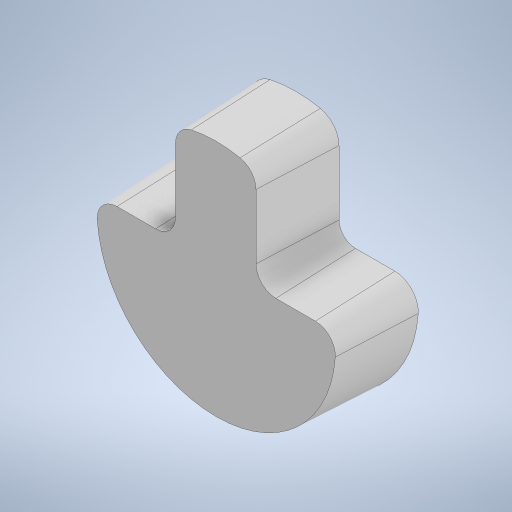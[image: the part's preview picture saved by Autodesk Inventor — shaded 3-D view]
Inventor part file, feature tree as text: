
AUTODESK INVENTOR PART (.ipt)
format: ipt  version: 2023 (Build 270158000, 158)  size: 267,264 bytes
history: native  units: in
note: dims shown in document units (in); Inventor stores cm internally (conversion verified against a paired STEP export)
features: extrude x1, draft x1, sketch x1
ambient origin geometry x8: Origin, YZ Plane, XZ Plane, XY Plane, X Axis, Y Axis, Z Axis, Center Point
bodies: Solid1 (feature_tree)
feature tree (3):
  extrude  "Extrusion1"  Depth=0.5in
  draft  "FaceDraft1"
  sketch  "Sketch1"  dims[d2=1.5in d3=0.25in d6=0.25in d7=0.5in d8=0.0in d11=0.625in d12=0.125in d13=0.0172in d10=0.5in]
